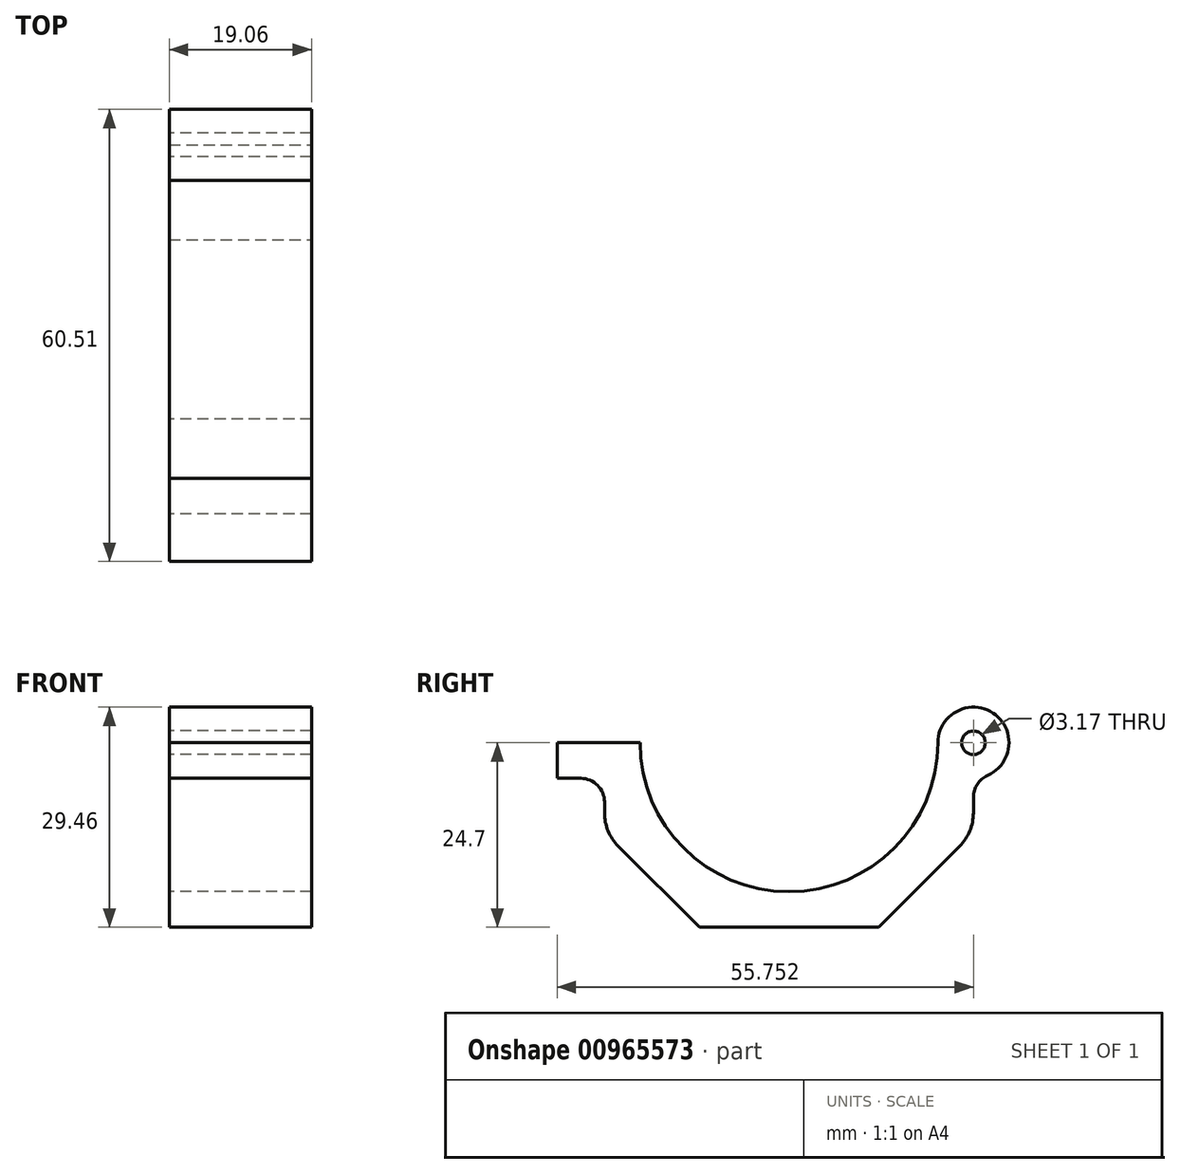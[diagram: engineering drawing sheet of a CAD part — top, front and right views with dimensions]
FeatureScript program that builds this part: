
annotation { "Feature Type Name" : "Feature", "Feature Type Description" : "" }
export const myFeature = defineFeature(function(context is Context, id is Id, definition is map)
    precondition{}
    {
        {
            var Q0;
            Q0=qCreatedBy(makeId("Right.planeOp"),FACE);
            var sketch = newSketch(context, id + "F0", { "sketchPlane" : qUnion([Q0])});
            skArc(sketch, "E0", {"start": v(-19.94, 0) * mm, "mid": v(0, -19.94) * mm, "end": v(19.94, 0) * mm});
            skCircle(sketch, "E1", {"center": v(24.7, 0) * mm, "radius": 1.59 * mm});
            skLineSegment(sketch, "E2", {"start": v(-19.94, 0) * mm, "end": v(-24.7, 0) * mm});
            skLineSegment(sketch, "E3", {"start": v(-24.7, -4.76) * mm, "end": v(-24.7, -24.7) * mm});
            skLineSegment(sketch, "E4", {"start": v(-24.7, -24.7) * mm, "end": v(24.7, -24.7) * mm});
            skLineSegment(sketch, "E5", {"start": v(24.7, -24.7) * mm, "end": v(24.7, -4.76) * mm});
            skArc(sketch, "E6", {"start": v(19.94, 0) * mm, "mid": v(28.07, 3.37) * mm, "end": v(24.7, -4.76) * mm});
            skLineSegment(sketch, "E7", {"start": v(19.94, 0) * mm, "end": v(24.7, 0) * mm, "construction": true});
            skLineSegment(sketch, "E8", {"start": v(0, -19.94) * mm, "end": v(0, -24.7) * mm, "construction": true});
            skLineSegment(sketch, "E9", {"start": v(-24.7, -4.76) * mm, "end": v(-31.05, -4.76) * mm});
            skLineSegment(sketch, "E10", {"start": v(-31.05, -4.76) * mm, "end": v(-31.05, 0) * mm});
            skLineSegment(sketch, "E11", {"start": v(-31.05, 0) * mm, "end": v(-24.7, 0) * mm});
            skSolve(sketch);
        }
        {
            var Q0;
            Q0 = qSketchRegion(id + "F0", true);
            extrude(context, id + "F1", {"entities" : qUnion([Q0]), "endBound" : BoundingType.SYMMETRIC, "depth" : 19.05 * mm, "offsetDistance" : 25.4 * mm});
        }
        {
            var Q0;
            Q0=makeQuery(id+"F1.opExtrude","SWEPT_EDGE",EDGE,{"disambiguationData":[OSD([sQuery(id+"F0.wireOp",EDGE,"E3"),sQuery(id+"F0.wireOp",EDGE,"E4")])]});
            var Q1;
            Q1=makeQuery(id+"F1.opExtrude","SWEPT_EDGE",EDGE,{"disambiguationData":[OSD([sQuery(id+"F0.wireOp",EDGE,"E4"),sQuery(id+"F0.wireOp",EDGE,"E5")])]});
            chamfer(context, id + "F2", {"entities" : qUnion([Q0, Q1]), "width" : 12.7 * mm, "tangentPropagation" : true});
        }
        {
            var Q0;
            Q0=makeQuery(id+"F1.opExtrude","SWEPT_EDGE",EDGE,{"disambiguationData":[OSD([sQuery(id+"F0.wireOp",EDGE,"E5"),sQuery(id+"F0.wireOp",EDGE,"E6")])]});
            var Q1;
            Q1=makeQuery(id+"F1.opExtrude","SWEPT_EDGE",EDGE,{"disambiguationData":[OSD([sQuery(id+"F0.wireOp",EDGE,"E3"),sQuery(id+"F0.wireOp",EDGE,"E9")])]});
            fillet(context, id + "F3", {"entities" : qUnion([Q0, Q1]), "radius" : 3.17 * mm, "tangentPropagation" : true, "allowEdgeOverflow" : false});
        }
        {
            var Q0;
            {var subQ0=sQuery(id+"F0.wireOp",EDGE,"E5");Q0=makeQuery(id+"F2.opChamfer","BLEND_EDGE",EDGE,{"blendedFrom":[makeQuery(id+"F1.opExtrude","SWEPT_EDGE",EDGE,{"disambiguationData":[OSD([sQuery(id+"F0.wireOp",EDGE,"E4"),subQ0])]}),makeQuery(id+"F1.opExtrude","SWEPT_FACE",FACE,{"disambiguationData":[OSD([subQ0])]})],"blendedInto":[makeQuery(id+"F1.opExtrude","SWEPT_FACE",FACE,{"disambiguationData":[OSD([subQ0])]})]});}
            var Q1;
            {var subQ0=sQuery(id+"F0.wireOp",EDGE,"E3");Q1=makeQuery(id+"F2.opChamfer","BLEND_EDGE",EDGE,{"blendedFrom":[makeQuery(id+"F1.opExtrude","SWEPT_EDGE",EDGE,{"disambiguationData":[OSD([subQ0,sQuery(id+"F0.wireOp",EDGE,"E4")])]}),makeQuery(id+"F1.opExtrude","SWEPT_FACE",FACE,{"disambiguationData":[OSD([subQ0])]})],"blendedInto":[makeQuery(id+"F1.opExtrude","SWEPT_FACE",FACE,{"disambiguationData":[OSD([subQ0])]})]});}
            fillet(context, id + "F4", {"entities" : qUnion([Q0, Q1]), "radius" : 6.35 * mm, "tangentPropagation" : true, "allowEdgeOverflow" : false});
        }
    });
